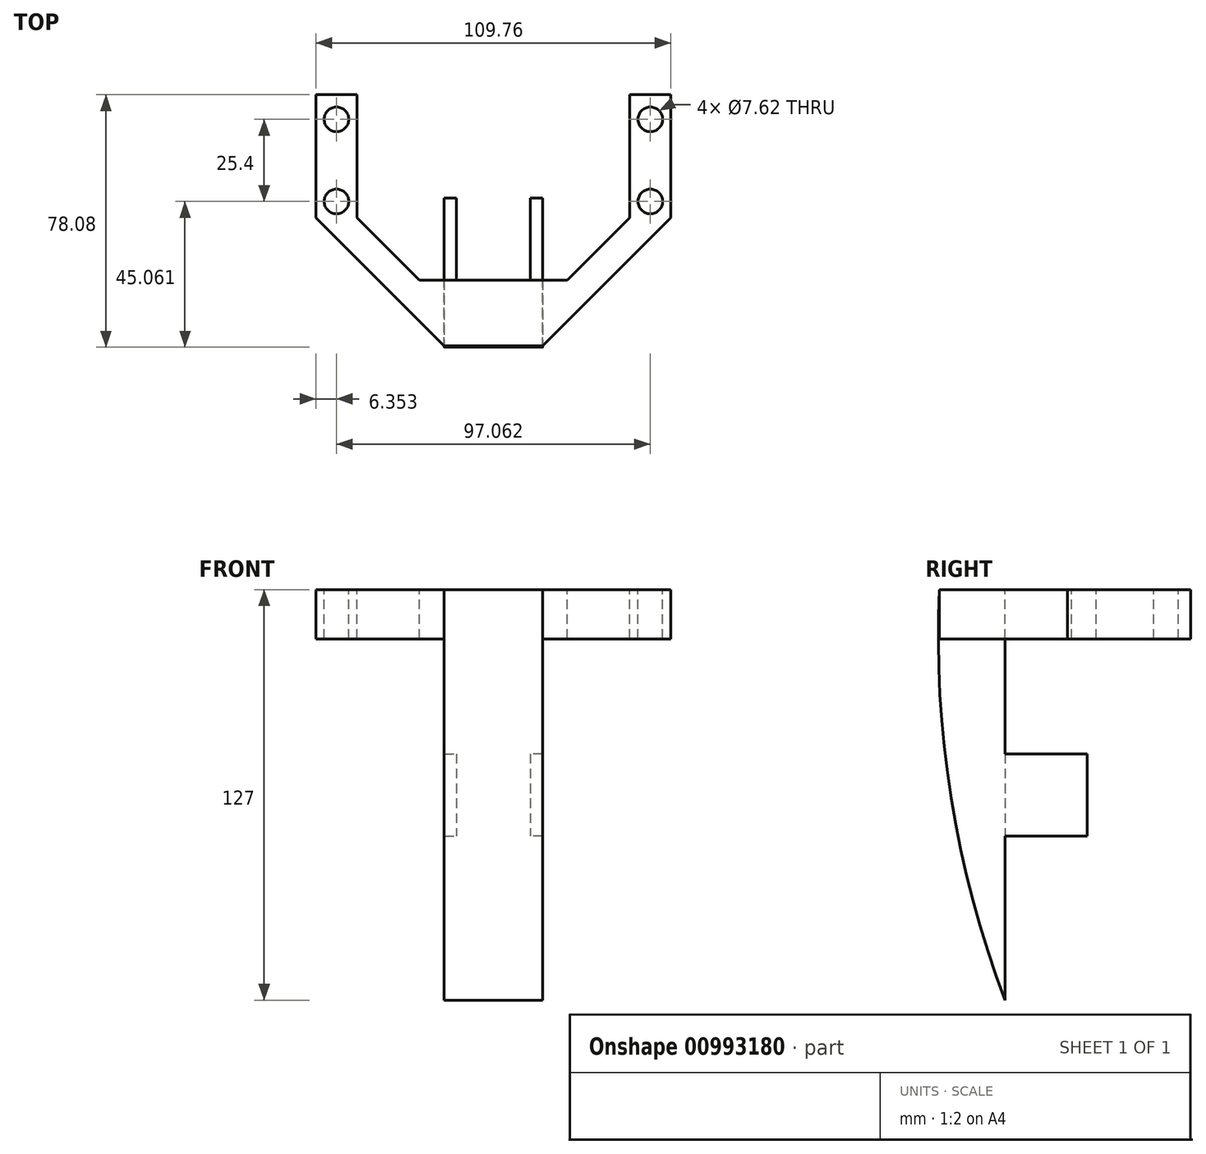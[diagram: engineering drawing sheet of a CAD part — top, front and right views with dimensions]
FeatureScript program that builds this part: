
annotation { "Feature Type Name" : "Feature", "Feature Type Description" : "" }
export const myFeature = defineFeature(function(context is Context, id is Id, definition is map)
    precondition{}
    {
        {
            var Q0;
            Q0=qCreatedBy(makeId("Front.planeOp"),FACE);
            var sketch = newSketch(context, id + "F0", { "sketchPlane" : qUnion([Q0])});
            skLineSegment(sketch, "E0.bottom", {"start": v(-55.75, 34.73) * mm, "end": v(-25.27, 34.73) * mm});
            skLineSegment(sketch, "E0.top", {"start": v(-55.75, -41.47) * mm, "end": v(-25.27, -41.47) * mm});
            skLineSegment(sketch, "E0.left", {"start": v(-55.75, 34.73) * mm, "end": v(-55.75, -41.47) * mm});
            skLineSegment(sketch, "E0.right", {"start": v(-25.27, 34.73) * mm, "end": v(-25.27, -41.47) * mm});
            skPoint(sketch, "E1.startSnap0", {"position": v(-55.75, -3.37) * mm});
            skPoint(sketch, "E2.startSnap0", {"position": v(-25.27, -3.37) * mm});
            skLineSegment(sketch, "E3.bottom", {"start": v(-25.27, 9.33) * mm, "end": v(-29.08, 9.33) * mm});
            skLineSegment(sketch, "E3.top", {"start": v(-25.27, -16.07) * mm, "end": v(-29.08, -16.07) * mm});
            skLineSegment(sketch, "E3.left", {"start": v(-25.27, 9.33) * mm, "end": v(-25.27, -16.07) * mm});
            skLineSegment(sketch, "E3.right", {"start": v(-29.08, 9.33) * mm, "end": v(-29.08, -16.07) * mm});
            skPoint(sketch, "E3.middle", {"position": v(-27.17, -3.37) * mm});
            skLineSegment(sketch, "E4.bottom", {"start": v(-55.75, 9.33) * mm, "end": v(-51.94, 9.33) * mm});
            skLineSegment(sketch, "E4.top", {"start": v(-55.75, -16.07) * mm, "end": v(-51.94, -16.07) * mm});
            skLineSegment(sketch, "E4.left", {"start": v(-55.75, 9.33) * mm, "end": v(-55.75, -16.07) * mm});
            skLineSegment(sketch, "E4.right", {"start": v(-51.94, 9.33) * mm, "end": v(-51.94, -16.07) * mm});
            skPoint(sketch, "E4.middle", {"position": v(-53.84, -3.37) * mm});
            skSolve(sketch);
        }
        {
            var Q0;
            Q0=makeQuery(id+"F0.imprint","IMPRINT",FACE,{"disambiguationData":[TD([[makeQuery(id+"F0.imprint","IMPRINT",EDGE,{"derivedFrom":sQuery(id+"F0.wireOp",EDGE,"E0.bottom")}),-1.0]])]});
            var Q1;
            Q1=makeQuery(id+"F0.imprint","IMPRINT",FACE,{"disambiguationData":[TD([[makeQuery(id+"F0.imprint","IMPRINT",EDGE,{"derivedFrom":sQuery(id+"F0.wireOp",EDGE,"E0.left")}),-1.0]])]});
            var Q2;
            Q2=makeQuery(id+"F0.imprint","IMPRINT",FACE,{"disambiguationData":[TD([[makeQuery(id+"F0.imprint","IMPRINT",EDGE,{"derivedFrom":sQuery(id+"F0.wireOp",EDGE,"E0.right")}),1.0]])]});
            extrude(context, id + "F1", {"entities" : qUnion([Q0, Q1, Q2]), "depth" : 7.62 * mm, "offsetDistance" : 25.4 * mm});
        }
        {
            var Q0;
            Q0=makeQuery(id+"F0.imprint","IMPRINT",FACE,{"disambiguationData":[TD([[makeQuery(id+"F0.imprint","IMPRINT",EDGE,{"derivedFrom":sQuery(id+"F0.wireOp",EDGE,"E4.bottom")}),-1.0]])]});
            var Q1;
            Q1=makeQuery(id+"F0.imprint","IMPRINT",FACE,{"disambiguationData":[TD([[makeQuery(id+"F0.imprint","IMPRINT",EDGE,{"derivedFrom":sQuery(id+"F0.wireOp",EDGE,"E3.bottom")}),1.0]])]});
            extrude(context, id + "F2", {"entities" : qUnion([Q0, Q1]), "operationType" : NewBodyOperationType.ADD, "oppositeDirection" : true, "depth" : 25.4 * mm, "offsetDistance" : 25.4 * mm, "hasSecondDirection" : true, "secondDirectionOppositeDirection" : false, "secondDirectionDepth" : 7.62 * mm});
        }
        {
            var Q0;
            {var subQ0=sQuery(id+"F0.wireOp",EDGE,"E3.left");var subQ1=sQuery(id+"F0.wireOp",EDGE,"E0.right");Q0=makeQuery(id+"F2.boolean.opBoolean","MERGE",FACE,{"derivedFrom":[makeQuery(id+"F1.opExtrude","SWEPT_FACE",FACE,{"disambiguationData":[OSD([subQ1]),TDD([makeQuery(id+"F0.imprint","IMPRINT",EDGE,{"disambiguationData":[TD([[makeQuery(id+"F0.imprint","INTERSECT",VERTEX,{"derivedFrom":[sQuery(id+"F0.wireOp",EDGE,"E0.bottom"),subQ1]}),-1.0]])],"derivedFrom":subQ1})])]}),makeQuery(id+"F1.opExtrude","SWEPT_FACE",FACE,{"disambiguationData":[OSD([subQ1]),TDD([makeQuery(id+"F0.imprint","IMPRINT",EDGE,{"disambiguationData":[TD([[makeQuery(id+"F0.imprint","INTERSECT",VERTEX,{"derivedFrom":[sQuery(id+"F0.wireOp",EDGE,"E0.top"),subQ1]}),1.0]])],"derivedFrom":subQ1})])]}),makeQuery(id+"F2.opExtrude","SWEPT_FACE",FACE,{"disambiguationData":[OSD([subQ0])]})]});}
            var sketch = newSketch(context, id + "F3", { "sketchPlane" : qUnion([Q0])});
            skLineSegment(sketch, "E5", {"start": v(0, 34.73) * mm, "end": v(0, 60.13) * mm});
            skLineSegment(sketch, "E6", {"start": v(0, 60.13) * mm, "end": v(-20.32, 60.13) * mm});
            skLineSegment(sketch, "E7", {"start": v(0, -41.47) * mm, "end": v(0, -66.87) * mm});
            skArc(sketch, "E8", {"start": v(-20.32, 60.13) * mm, "mid": v(-16.7, -4.42) * mm, "end": v(0, -66.87) * mm});
            skSolve(sketch);
        }
        {
            var Q0;
            Q0=makeQuery(id+"F3.imprint","IMPRINT",FACE,{"disambiguationData":[TD([[makeQuery(id+"F3.imprint","IMPRINT",EDGE,{"derivedFrom":sQuery(id+"F3.wireOp",EDGE,"E5")}),1.0]])]});
            extrude(context, id + "F4", {"entities" : qUnion([Q0]), "operationType" : NewBodyOperationType.ADD, "oppositeDirection" : true, "depth" : 30.48 * mm, "offsetDistance" : 25.4 * mm});
        }
        {
            var Q0;
            Q0=makeQuery(id+"F4.opExtrude","SWEPT_FACE",FACE,{"disambiguationData":[OSD([sQuery(id+"F3.wireOp",EDGE,"E6")])]});
            var sketch = newSketch(context, id + "F5", { "sketchPlane" : qUnion([Q0])});
            skLineSegment(sketch, "E9", {"start": v(-55.75, -20.32) * mm, "end": v(-82.69, 6.62) * mm});
            skLineSegment(sketch, "E10", {"start": v(-55.75, 0) * mm, "end": v(-63.37, 0) * mm});
            skLineSegment(sketch, "E11", {"start": v(-25.27, 0) * mm, "end": v(-17.65, 0) * mm});
            skLineSegment(sketch, "E12", {"start": v(-25.27, -20.32) * mm, "end": v(1.67, 6.62) * mm});
            skLineSegment(sketch, "E13", {"start": v(-82.69, 19.32) * mm, "end": v(-63.37, 0) * mm});
            skLineSegment(sketch, "E14", {"start": v(1.67, 19.32) * mm, "end": v(-17.65, 0) * mm});
            skLineSegment(sketch, "E15", {"start": v(-82.69, 19.32) * mm, "end": v(-95.39, 19.32) * mm});
            skLineSegment(sketch, "E16", {"start": v(1.67, 6.62) * mm, "end": v(14.37, 19.32) * mm});
            skLineSegment(sketch, "E17", {"start": v(14.37, 19.32) * mm, "end": v(1.67, 19.32) * mm});
            skLineSegment(sketch, "E18", {"start": v(-82.69, 6.62) * mm, "end": v(-95.39, 19.32) * mm});
            skSolve(sketch);
        }
        {
            var Q0;
            Q0=makeQuery(id+"F5.imprint","IMPRINT",FACE,{"disambiguationData":[TD([[makeQuery(id+"F5.imprint","IMPRINT",EDGE,{"derivedFrom":sQuery(id+"F5.wireOp",EDGE,"E11")}),-1.0]])]});
            var Q1;
            Q1=makeQuery(id+"F5.imprint","IMPRINT",FACE,{"disambiguationData":[TD([[makeQuery(id+"F5.imprint","IMPRINT",EDGE,{"derivedFrom":sQuery(id+"F5.wireOp",EDGE,"E9")}),-1.0]])]});
            extrude(context, id + "F6", {"entities" : qUnion([Q0, Q1]), "operationType" : NewBodyOperationType.ADD, "oppositeDirection" : true, "depth" : 15.24 * mm, "offsetDistance" : 25.4 * mm});
        }
        {
            var Q0;
            Q0=makeQuery(id+"F6.opExtrude","SWEPT_FACE",FACE,{"disambiguationData":[OSD([sQuery(id+"F5.wireOp",EDGE,"E17")])]});
            var Q1;
            Q1=makeQuery(id+"F6.opExtrude","SWEPT_FACE",FACE,{"disambiguationData":[OSD([sQuery(id+"F5.wireOp",EDGE,"E15")])]});
            extrude(context, id + "F7", {"entities" : qUnion([Q0, Q1]), "operationType" : NewBodyOperationType.ADD, "depth" : 38.1 * mm, "offsetDistance" : 25.4 * mm});
        }
        {
            var Q0;
            {var subQ0=sQuery(id+"F5.wireOp",EDGE,"E17");var subQ1=sQuery(id+"F5.wireOp",EDGE,"E15");var subQ2=sQuery(id+"F3.wireOp",EDGE,"E6");Q0=makeQuery(id+"F7.boolean.opBoolean","MERGE",FACE,{"derivedFrom":[makeQuery(id+"F6.boolean.opBoolean","MERGE",FACE,{"derivedFrom":[makeQuery(id+"F4.opExtrude","SWEPT_FACE",FACE,{"disambiguationData":[OSD([subQ2])]}),makeQuery(id+"F6.opExtrude","CAP_FACE",FACE,{"disambiguationData":[OSD([subQ2,sQuery(id+"F5.wireOp",EDGE,"E9"),sQuery(id+"F5.wireOp",EDGE,"E10"),sQuery(id+"F5.wireOp",EDGE,"E13"),subQ1,sQuery(id+"F5.wireOp",EDGE,"E18")])],"isStart":true}),makeQuery(id+"F6.opExtrude","CAP_FACE",FACE,{"disambiguationData":[OSD([subQ2,sQuery(id+"F5.wireOp",EDGE,"E11"),sQuery(id+"F5.wireOp",EDGE,"E12"),sQuery(id+"F5.wireOp",EDGE,"E14"),sQuery(id+"F5.wireOp",EDGE,"E16"),subQ0])],"isStart":true})]}),makeQuery(id+"F7.opExtrude","SWEPT_FACE",FACE,{"disambiguationData":[OSD([subQ1]),TDD([makeQuery(id+"F6.opExtrude","CAP_EDGE",EDGE,{"disambiguationData":[OSD([subQ1])],"isStart":true})])]}),makeQuery(id+"F7.opExtrude","SWEPT_FACE",FACE,{"disambiguationData":[OSD([subQ0]),TDD([makeQuery(id+"F6.opExtrude","CAP_EDGE",EDGE,{"disambiguationData":[OSD([subQ0])],"isStart":true})])]})]});}
            var sketch = newSketch(context, id + "F8", { "sketchPlane" : qUnion([Q0])});
            skCircle(sketch, "E19", {"center": v(8.02, 49.8) * mm, "radius": 3.81 * mm});
            skPoint(sketch, "E19.centerSnap0", {"position": v(8.02, 57.42) * mm});
            skCircle(sketch, "E20", {"center": v(8.02, 24.4) * mm, "radius": 3.81 * mm});
            skCircle(sketch, "E21", {"center": v(-89.04, 49.8) * mm, "radius": 3.81 * mm});
            skPoint(sketch, "E21.centerSnap0", {"position": v(-89.04, 57.42) * mm});
            skCircle(sketch, "E22", {"center": v(-89.04, 24.4) * mm, "radius": 3.81 * mm});
            skSolve(sketch);
        }
        {
            var Q0;
            Q0=makeQuery(id+"F8.imprint","IMPRINT",FACE,{"disambiguationData":[TD([[makeQuery(id+"F8.imprint","IMPRINT",EDGE,{"derivedFrom":sQuery(id+"F8.wireOp",EDGE,"E21")}),1.0]])]});
            var Q1;
            Q1=makeQuery(id+"F8.imprint","IMPRINT",FACE,{"disambiguationData":[TD([[makeQuery(id+"F8.imprint","IMPRINT",EDGE,{"derivedFrom":sQuery(id+"F8.wireOp",EDGE,"E22")}),1.0]])]});
            var Q2;
            Q2=makeQuery(id+"F8.imprint","IMPRINT",FACE,{"disambiguationData":[TD([[makeQuery(id+"F8.imprint","IMPRINT",EDGE,{"derivedFrom":sQuery(id+"F8.wireOp",EDGE,"E19")}),1.0]])]});
            var Q3;
            Q3=makeQuery(id+"F8.imprint","IMPRINT",FACE,{"disambiguationData":[TD([[makeQuery(id+"F8.imprint","IMPRINT",EDGE,{"derivedFrom":sQuery(id+"F8.wireOp",EDGE,"E20")}),1.0]])]});
            extrude(context, id + "F9", {"entities" : qUnion([Q0, Q1, Q2, Q3]), "operationType" : NewBodyOperationType.REMOVE, "oppositeDirection" : true, "depth" : 25.4 * mm, "offsetDistance" : 25.4 * mm});
        }
    });
